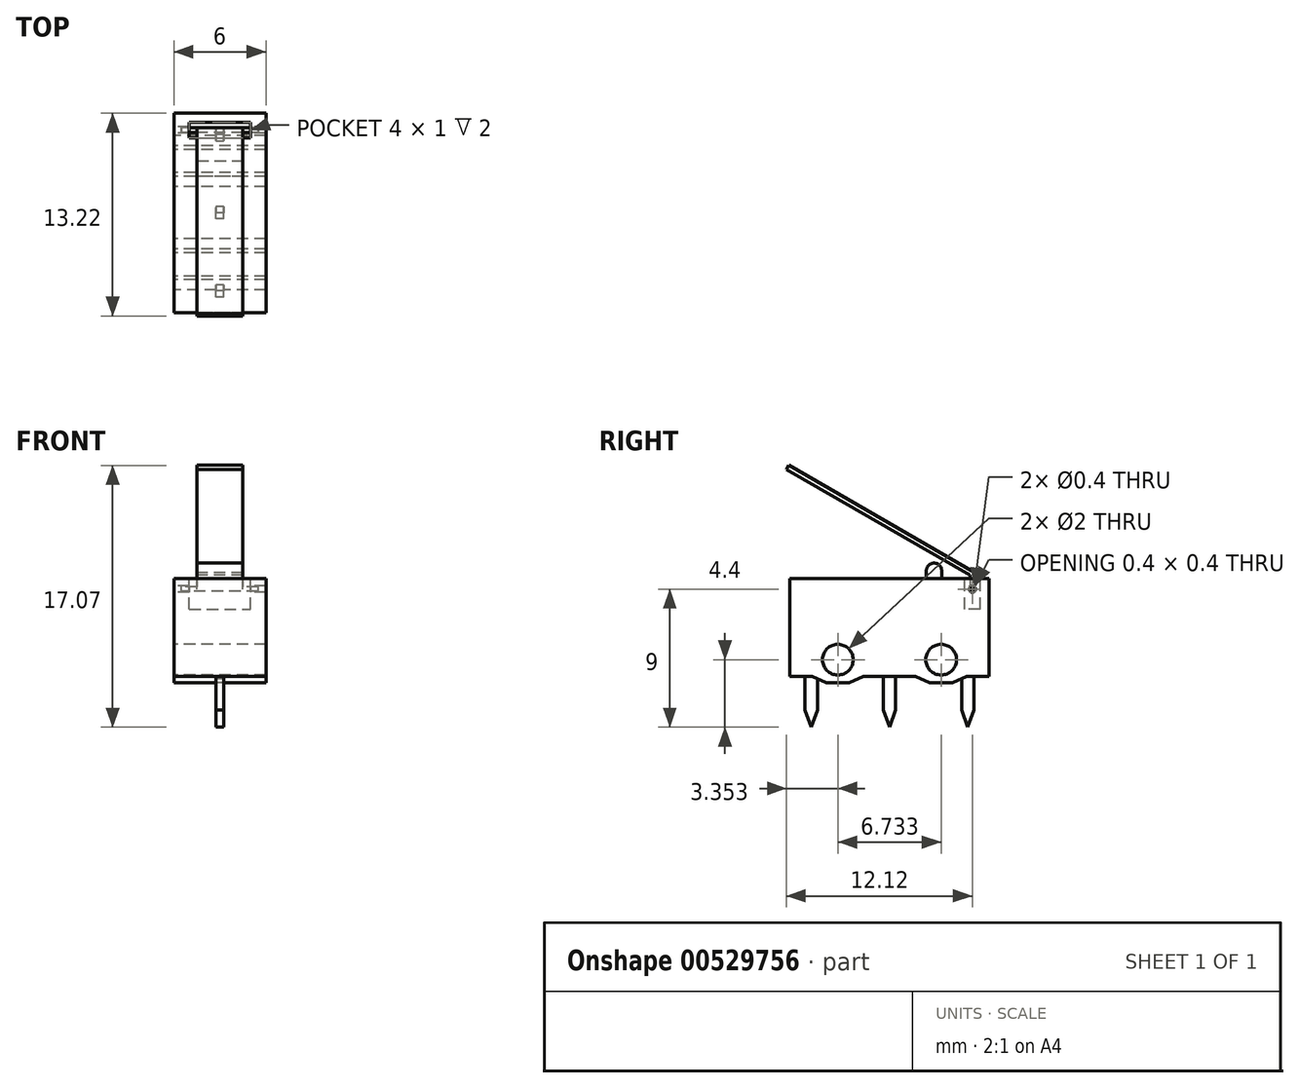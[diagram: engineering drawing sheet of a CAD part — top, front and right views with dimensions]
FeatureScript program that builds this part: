
annotation { "Feature Type Name" : "Feature", "Feature Type Description" : "" }
export const myFeature = defineFeature(function(context is Context, id is Id, definition is map)
    precondition{}
    {
        {
            var Q0;
            Q0=qCreatedBy(makeId("Right.planeOp"),FACE);
            var sketch = newSketch(context, id + "F0", { "sketchPlane" : qUnion([Q0])});
            skLineSegment(sketch, "E0", {"start": v(-6.5, 3.2) * mm, "end": v(-6.5, -3.2) * mm});
            skLineSegment(sketch, "E1", {"start": v(-6.5, -3.2) * mm, "end": v(-5.03, -3.2) * mm});
            skLineSegment(sketch, "E2", {"start": v(-5.03, -3.2) * mm, "end": v(-4.12, -3.6) * mm});
            skLineSegment(sketch, "E3", {"start": v(-4.12, -3.6) * mm, "end": v(-2.62, -3.6) * mm});
            skLineSegment(sketch, "E4", {"start": v(-2.62, -3.6) * mm, "end": v(-1.7, -3.2) * mm});
            skLineSegment(sketch, "E5", {"start": v(-1.7, -3.2) * mm, "end": v(0, -3.2) * mm});
            skLineSegment(sketch, "E6", {"start": v(-6.5, 3.2) * mm, "end": v(0, 3.2) * mm});
            skLineSegment(sketch, "E7.MirrorCS", {"start": v(5.03, -3.2) * mm, "end": v(4.12, -3.6) * mm});
            skLineSegment(sketch, "E8.MirrorCS", {"start": v(2.62, -3.6) * mm, "end": v(1.7, -3.2) * mm});
            skLineSegment(sketch, "E9.MirrorCS", {"start": v(4.12, -3.6) * mm, "end": v(2.62, -3.6) * mm});
            skLineSegment(sketch, "E10.MirrorCS", {"start": v(6.5, 3.2) * mm, "end": v(6.5, -3.2) * mm});
            skLineSegment(sketch, "E11.MirrorCS", {"start": v(6.5, 3.2) * mm, "end": v(0, 3.2) * mm});
            skLineSegment(sketch, "E12.MirrorCS", {"start": v(6.5, -3.2) * mm, "end": v(5.03, -3.2) * mm});
            skLineSegment(sketch, "E13.MirrorCS", {"start": v(1.7, -3.2) * mm, "end": v(0, -3.2) * mm});
            skLineSegment(sketch, "E14", {"start": v(-6.5, 0) * mm, "end": v(6.5, 0) * mm, "construction": true});
            skCircle(sketch, "E15", {"center": v(-3.37, -2.1) * mm, "radius": 1 * mm});
            skLineSegment(sketch, "E16", {"start": v(-3.37, -3.6) * mm, "end": v(-3.37, 0) * mm, "construction": true});
            skCircle(sketch, "E17.MirrorC", {"center": v(3.37, -2.1) * mm, "radius": 1 * mm});
            skCircle(sketch, "E18", {"center": v(5.4, 2.5) * mm, "radius": 0.2 * mm});
            skLineSegment(sketch, "E19", {"start": v(5.4, 2.5) * mm, "end": v(5.4, 5.04) * mm, "construction": true});
            skSolve(sketch);
        }
        {
            var Q0;
            Q0=makeQuery(id+"F0.imprint","IMPRINT",FACE,{"disambiguationData":[TD([[makeQuery(id+"F0.imprint","IMPRINT",EDGE,{"derivedFrom":sQuery(id+"F0.wireOp",EDGE,"E0")}),1.0]])]});
            extrude(context, id + "F1", {"entities" : qUnion([Q0]), "depth" : 6 * mm, "offsetDistance" : 25 * mm, "symmetric" : true});
        }
        {
            var Q0;
            Q0=qCreatedBy(makeId("Right.planeOp"),FACE);
            var sketch = newSketch(context, id + "F2", { "sketchPlane" : qUnion([Q0])});
            skLineSegment(sketch, "E20", {"start": v(-5.5, -3.2) * mm, "end": v(-5.5, -5.37) * mm});
            skLineSegment(sketch, "E21", {"start": v(-5.5, -5.37) * mm, "end": v(-5.1, -6.5) * mm});
            skLineSegment(sketch, "E22", {"start": v(-5.1, -6.5) * mm, "end": v(-5.1, -3.2) * mm, "construction": true});
            skLineSegment(sketch, "E23.MirrorCS", {"start": v(-4.7, -3.2) * mm, "end": v(-4.7, -5.37) * mm});
            skLineSegment(sketch, "E24.MirrorCS", {"start": v(-4.7, -5.37) * mm, "end": v(-5.1, -6.5) * mm});
            skLineSegment(sketch, "E25", {"start": v(-5.5, -3.2) * mm, "end": v(-4.7, -3.2) * mm});
            skLineSegment(sketch, "E26.1.0.0", {"start": v(0.4, -5.37) * mm, "end": v(0, -6.5) * mm});
            skLineSegment(sketch, "E26.1.0.1", {"start": v(0.4, -3.2) * mm, "end": v(0.4, -5.37) * mm});
            skLineSegment(sketch, "E26.1.0.2", {"start": v(0, -6.5) * mm, "end": v(0, -3.2) * mm, "construction": true});
            skLineSegment(sketch, "E26.1.0.3", {"start": v(-0.4, -5.37) * mm, "end": v(0, -6.5) * mm});
            skLineSegment(sketch, "E26.1.0.4", {"start": v(-0.4, -3.2) * mm, "end": v(-0.4, -5.37) * mm});
            skLineSegment(sketch, "E26.1.0.5", {"start": v(-0.4, -3.2) * mm, "end": v(0.4, -3.2) * mm});
            skLineSegment(sketch, "E26.2.0.0", {"start": v(5.5, -5.37) * mm, "end": v(5.1, -6.5) * mm});
            skLineSegment(sketch, "E26.2.0.1", {"start": v(5.5, -3.2) * mm, "end": v(5.5, -5.37) * mm});
            skLineSegment(sketch, "E26.2.0.2", {"start": v(5.1, -6.5) * mm, "end": v(5.1, -3.2) * mm, "construction": true});
            skLineSegment(sketch, "E26.2.0.3", {"start": v(4.7, -5.37) * mm, "end": v(5.1, -6.5) * mm});
            skLineSegment(sketch, "E26.2.0.4", {"start": v(4.7, -3.2) * mm, "end": v(4.7, -5.37) * mm});
            skLineSegment(sketch, "E26.2.0.5", {"start": v(4.7, -3.2) * mm, "end": v(5.5, -3.2) * mm});
            skLineSegment(sketch, "E26.direction1", {"start": v(-5.1, -6.5) * mm, "end": v(0, -6.5) * mm, "construction": true});
            skSolve(sketch);
        }
        {
            var Q0;
            Q0=makeQuery(id+"F2.imprint","IMPRINT",FACE,{"disambiguationData":[TD([[makeQuery(id+"F2.imprint","IMPRINT",EDGE,{"derivedFrom":sQuery(id+"F2.wireOp",EDGE,"E20")}),1.0]])]});
            var Q1;
            Q1=makeQuery(id+"F2.imprint","IMPRINT",FACE,{"disambiguationData":[TD([[makeQuery(id+"F2.imprint","IMPRINT",EDGE,{"derivedFrom":sQuery(id+"F2.wireOp",EDGE,"E26.1.0.0")}),-1.0]])]});
            var Q2;
            Q2=makeQuery(id+"F2.imprint","IMPRINT",FACE,{"disambiguationData":[TD([[makeQuery(id+"F2.imprint","IMPRINT",EDGE,{"derivedFrom":sQuery(id+"F2.wireOp",EDGE,"E26.2.0.0")}),-1.0]])]});
            extrude(context, id + "F3", {"entities" : qUnion([Q0, Q1, Q2]), "operationType" : NewBodyOperationType.ADD, "depth" : 0.5 * mm, "offsetDistance" : 25 * mm, "symmetric" : true});
        }
        {
            var Q0;
            Q0=makeQuery(id+"F1.opExtrude","SWEPT_FACE",FACE,{"disambiguationData":[OSD([sQuery(id+"F0.wireOp",EDGE,"E6"),sQuery(id+"F0.wireOp",EDGE,"E11.MirrorCS")])]});
            var sketch = newSketch(context, id + "F4", { "sketchPlane" : qUnion([Q0])});
            skLineSegment(sketch, "E27", {"start": v(0, 5.9) * mm, "end": v(-2, 5.9) * mm});
            skLineSegment(sketch, "E28", {"start": v(-2, 5.9) * mm, "end": v(-2, 4.9) * mm});
            skLineSegment(sketch, "E29", {"start": v(-2, 4.9) * mm, "end": v(0, 4.9) * mm});
            skLineSegment(sketch, "E30.MirrorCS", {"start": v(0, 5.9) * mm, "end": v(2, 5.9) * mm});
            skLineSegment(sketch, "E31.MirrorCS", {"start": v(2, 5.9) * mm, "end": v(2, 4.9) * mm});
            skLineSegment(sketch, "E32.MirrorCS", {"start": v(2, 4.9) * mm, "end": v(0, 4.9) * mm});
            skLineSegment(sketch, "E33", {"start": v(-2, 5.4) * mm, "end": v(2, 5.4) * mm, "construction": true});
            skLineSegment(sketch, "E34", {"start": v(0, 3.4) * mm, "end": v(-1.5, 3.4) * mm});
            skLineSegment(sketch, "E35", {"start": v(-1.5, 3.4) * mm, "end": v(-1.5, 2.4) * mm});
            skLineSegment(sketch, "E36", {"start": v(-1.5, 2.4) * mm, "end": v(0, 2.4) * mm});
            skLineSegment(sketch, "E37.MirrorCS", {"start": v(0, 3.4) * mm, "end": v(1.5, 3.4) * mm});
            skLineSegment(sketch, "E38.MirrorCS", {"start": v(1.5, 3.4) * mm, "end": v(1.5, 2.4) * mm});
            skLineSegment(sketch, "E39.MirrorCS", {"start": v(1.5, 2.4) * mm, "end": v(0, 2.4) * mm});
            skSolve(sketch);
        }
        {
            var Q0;
            Q0=makeQuery(id+"F4.imprint","IMPRINT",FACE,{"disambiguationData":[TD([[makeQuery(id+"F4.imprint","IMPRINT",EDGE,{"derivedFrom":sQuery(id+"F4.wireOp",EDGE,"E27")}),1.0]])]});
            var Q1;
            Q1=makeQuery(id+"F1.opExtrude","SWEPT_FACE",FACE,{"disambiguationData":[OSD([sQuery(id+"F0.wireOp",EDGE,"E18")])]});
            extrude(context, id + "F5", {"entities" : qUnion([Q0]), "operationType" : NewBodyOperationType.REMOVE, "oppositeDirection" : true, "depth" : 2 * mm, "endBoundEntityFace" : qUnion([Q1]), "offsetDistance" : 25 * mm});
        }
        {
            var Q0;
            Q0=makeQuery(id+"F4.imprint","IMPRINT",FACE,{"disambiguationData":[TD([[makeQuery(id+"F4.imprint","IMPRINT",EDGE,{"derivedFrom":sQuery(id+"F4.wireOp",EDGE,"E34")}),1.0]])]});
            extrude(context, id + "F6", {"entities" : qUnion([Q0]), "operationType" : NewBodyOperationType.ADD, "depth" : 1 * mm, "offsetDistance" : 25 * mm});
        }
        {
            var Q0;
            Q0=makeQuery(id+"F6.opExtrude","CAP_EDGE",EDGE,{"disambiguationData":[OSD([sQuery(id+"F4.wireOp",EDGE,"E34"),sQuery(id+"F4.wireOp",EDGE,"E37.MirrorCS")])],"isStart":false});
            var Q1;
            Q1=makeQuery(id+"F6.opExtrude","CAP_EDGE",EDGE,{"disambiguationData":[OSD([sQuery(id+"F4.wireOp",EDGE,"E36"),sQuery(id+"F4.wireOp",EDGE,"E39.MirrorCS")])],"isStart":false});
            fillet(context, id + "F7", {"entities" : qUnion([Q0, Q1]), "radius" : 0.5 * mm, "tangentPropagation" : true, "allowEdgeOverflow" : false});
        }
        {
            var Q0;
            Q0=qCreatedBy(makeId("Right.planeOp"),FACE);
            var sketch = newSketch(context, id + "F8", { "sketchPlane" : qUnion([Q0])});
            skCircle(sketch, "E40", {"center": v(5.4, 2.5) * mm, "radius": 0.15 * mm});
            skLineSegment(sketch, "E41", {"start": v(5.55, 2.5) * mm, "end": v(5.55, 3.57) * mm});
            skLineSegment(sketch, "E42", {"start": v(5.55, 3.57) * mm, "end": v(-6.57, 10.57) * mm});
            skLineSegment(sketch, "E43", {"start": v(-6.57, 10.57) * mm, "end": v(-6.72, 10.31) * mm});
            skLineSegment(sketch, "E44", {"start": v(-6.72, 10.31) * mm, "end": v(5.25, 3.4) * mm});
            skLineSegment(sketch, "E45", {"start": v(5.25, 3.4) * mm, "end": v(5.25, 2.5) * mm});
            skSolve(sketch);
        }
        {
            var Q0;
            {var subQ0=sQuery(id+"F8.wireOp",EDGE,"E41");Q0=makeQuery(id+"F8.imprint","IMPRINT",FACE,{"disambiguationData":[TD([[makeQuery(id+"F8.imprint","IMPRINT",EDGE,{"derivedFrom":subQ0}),1.0]])]});}
            extrude(context, id + "F9", {"entities" : qUnion([Q0]), "depth" : 3 * mm, "offsetDistance" : 25 * mm, "symmetric" : true});
        }
        {
            var Q0;
            {var subQ0=sQuery(id+"F8.wireOp",EDGE,"E40");var subQ1=makeQuery(id+"F8.imprint","INTERSECT",VERTEX,{"derivedFrom":[subQ0,sQuery(id+"F8.wireOp",EDGE,"E41")]});Q0=makeQuery(id+"F8.imprint","IMPRINT",FACE,{"disambiguationData":[TD([[makeQuery(id+"F8.imprint","IMPRINT",EDGE,{"disambiguationData":[TD([[subQ1,-1.0]])],"derivedFrom":subQ0}),1.0]])]});}
            extrude(context, id + "F10", {"entities" : qUnion([Q0]), "operationType" : NewBodyOperationType.ADD, "depth" : 5 * mm, "offsetDistance" : 25 * mm, "symmetric" : true});
        }
    });
